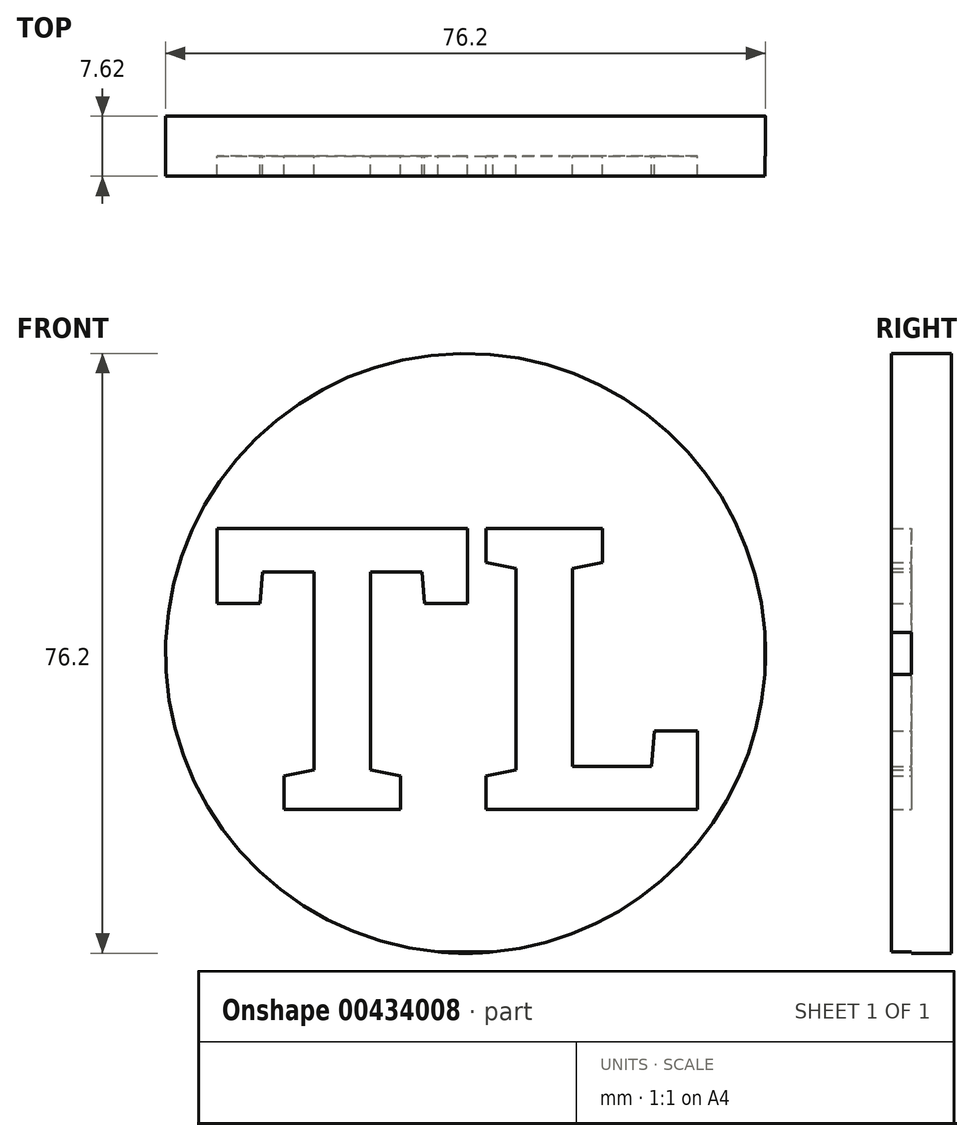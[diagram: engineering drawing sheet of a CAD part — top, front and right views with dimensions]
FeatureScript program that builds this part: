
annotation { "Feature Type Name" : "Feature", "Feature Type Description" : "" }
export const myFeature = defineFeature(function(context is Context, id is Id, definition is map)
    precondition{}
    {
        {
            var Q0;
            Q0=qCreatedBy(makeId("Front.planeOp"),FACE);
            var sketch = newSketch(context, id + "F0", { "sketchPlane" : qUnion([Q0])});
            skCircle(sketch, "E0", {"center": v(0, 0) * mm, "radius": 38.1 * mm});
            skLineSegment(sketch, "E1.bottom", {"start": v(-38.2, -37.94) * mm, "end": v(38, -37.94) * mm});
            skLineSegment(sketch, "E1.top", {"start": v(-38.2, 38.26) * mm, "end": v(38, 38.26) * mm});
            skLineSegment(sketch, "E1.left", {"start": v(-38.2, -37.94) * mm, "end": v(-38.2, 38.26) * mm});
            skLineSegment(sketch, "E1.right", {"start": v(38, -37.94) * mm, "end": v(38, 38.26) * mm});
            skText(sketch, "E2", { "text": "TL", "fontName": "RobotoSlab-Bold.ttf"});
            const initialGuessF0  = {"E2": [-0.03252, -0.01985, 1, 0, 0.03614]};
            skSetInitialGuess(sketch, initialGuessF0);
            skSolve(sketch);
        }
        {
            var Q0;
            Q0=makeQuery(id+"F0.imprint","IMPRINT",FACE,{"disambiguationData":[TD([[makeQuery(id+"F0.imprint","IMPRINT",EDGE,{"derivedFrom":sQuery(id+"F0.wireOp",EDGE,"E2.sketch_text.stroke-0")}),1.0]])]});
            extrude(context, id + "F1", {"entities" : qUnion([Q0]), "depth" : 2.54 * mm});
        }
        {
            var Q0;
            Q0=qCreatedBy(makeId("Front.planeOp"),FACE);
            var sketch = newSketch(context, id + "F2", { "sketchPlane" : qUnion([Q0])});
            skCircle(sketch, "E3", {"center": v(0, 0) * mm, "radius": 38.1 * mm});
            skSolve(sketch);
        }
        {
            var Q0;
            Q0=makeQuery(id+"F2.imprint","IMPRINT",FACE,{"disambiguationData":[TD([[makeQuery(id+"F2.imprint","IMPRINT",EDGE,{"derivedFrom":sQuery(id+"F2.wireOp",EDGE,"E3")}),1.0]])]});
            extrude(context, id + "F3", {"entities" : qUnion([Q0]), "operationType" : NewBodyOperationType.ADD, "oppositeDirection" : true, "depth" : 5.08 * mm});
        }
    });
